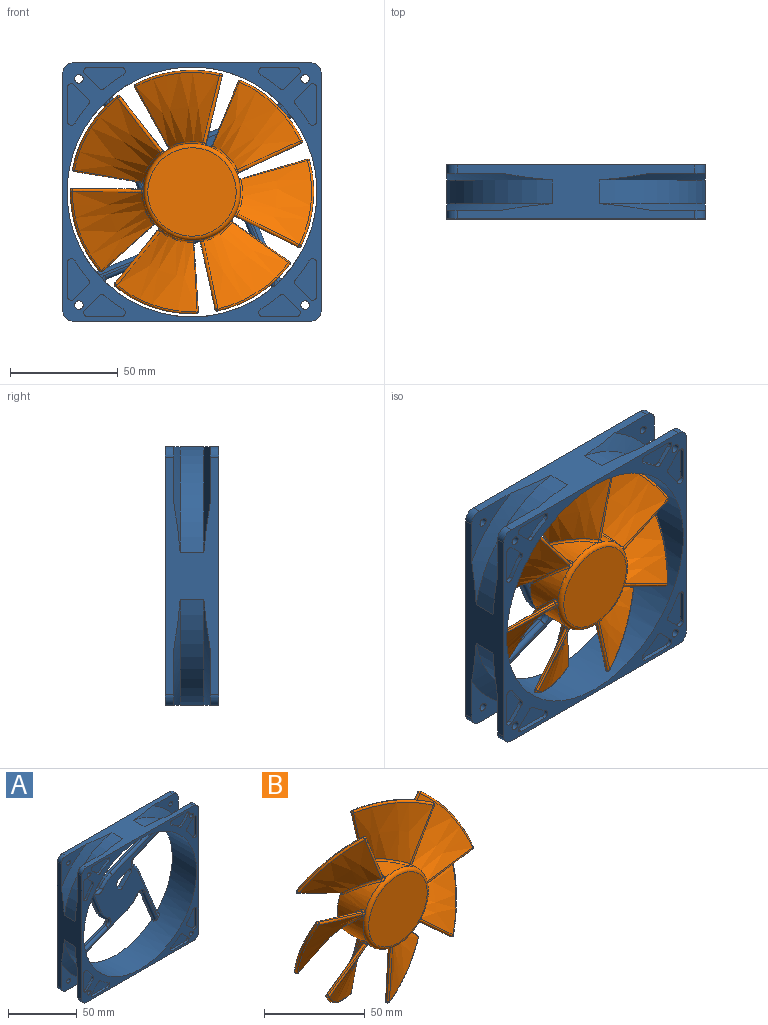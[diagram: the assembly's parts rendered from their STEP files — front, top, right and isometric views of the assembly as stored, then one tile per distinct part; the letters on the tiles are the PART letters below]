
ASSEMBLY  parts=2 mates=1
PART A: 223 faces, bbox 135.7x25x135.7 mm
  f0: plane 88.49x86.45mm, normal (0,-1,0), area 1656.3mm2, adj f15,f184,f185,f186,f187,f196,f197,f198
  f1: plane 120x120mm, normal (0,1,0), area 4802mm2, adj f2,f3,f5,f11,f12,f13,f14,f15
  f2: plane 110x25mm, normal (1,0,0), area 1352.3mm2, adj f1,f6,f23,f24,f25,f26,f27,f28
  f3: plane 6.72x2mm, normal (-1,0,0), area 13.4mm2, adj f1,f4,f35,f192
  f4: plane 65.36x42.4mm, normal (0,1,0), area 561.7mm2, adj f3,f5,f32,f33,f34,f35,f36,f182
  f5: cylinder r=2mm len=2mm, axis (0,1,0), area 1.5mm2, adj f1,f4,f32,f183
  f6: plane 120x120mm, normal (0,-1,0), area 2727.1mm2, adj f2,f7,f8,f9,f10,f12,f13,f14
  f7: cylinder r=2mm len=4mm, axis (0,1,0), area 50.3mm2, adj f6,f31
  f8: cylinder r=2mm len=4mm, axis (0,1,0), area 50.3mm2, adj f6,f26
  f9: cylinder r=2mm len=4mm, axis (0,1,0), area 50.3mm2, adj f6,f24
  f10: cylinder r=2mm len=4mm, axis (0,1,0), area 50.3mm2, adj f6,f21
  f11: plane 11.44x4mm, normal (1,0,0), area 45.8mm2, adj f1,f27,f142,f193
  f12: plane 110x25mm, normal (0,0,1), area 1413.4mm2, adj f1,f6,f26,f27,f28,f29,f30,f31
  f13: plane 110x25mm, normal (-1,0,0), area 1413.4mm2, adj f1,f6,f20,f21,f22,f29,f30,f31
  f14: plane 110x25mm, normal (0,0,-1), area 1413.4mm2, adj f1,f6,f20,f21,f22,f23,f24,f25
  f15: cylinder r=58mm len=116mm, axis (0,1,0), area 8990.7mm2, adj f0,f1,f6,f174,f175,f176,f177,f178
  f16: cylinder r=2mm len=4mm, axis (0,1,0), area 50.3mm2, adj f1,f30
  f17: cylinder r=2mm len=4mm, axis (0,1,0), area 50.3mm2, adj f1,f27
  f18: cylinder r=2mm len=4mm, axis (0,1,0), area 50.3mm2, adj f1,f23
  f19: cylinder r=2mm len=4mm, axis (0,1,0), area 50.3mm2, adj f1,f20
  f20: plane 25.93x25.93mm, normal (0,-1,0), area 257.3mm2, adj f13,f14,f19,f144,f151
  f21: plane 25.93x25.93mm, normal (0,1,0), area 257.3mm2, adj f10,f13,f14,f148,f154
  f22: cylinder r=61mm len=49mm, axis (0,1,0), area 810.7mm2, adj f13,f14,f151,f154
  f23: plane 25.93x25.93mm, normal (0,-1,0), area 257.3mm2, adj f2,f14,f18,f145,f152
  f24: plane 25.93x25.93mm, normal (0,1,0), area 257.3mm2, adj f2,f9,f14,f149,f155
  f25: cylinder r=61mm len=49mm, axis (0,1,0), area 810.7mm2, adj f2,f14,f152,f155
  f26: plane 25.93x25.93mm, normal (0,1,0), area 257.3mm2, adj f2,f8,f12,f146,f156
  f27: plane 25.93x25.93mm, normal (0,-1,0), area 240.5mm2, adj f2,f11,f12,f17,f142,f153,f191,f192
  f28: cylinder r=61mm len=49mm, axis (0,1,0), area 810.7mm2, adj f2,f12,f153,f156
  f29: cylinder r=61mm len=49mm, axis (0,1,0), area 810.7mm2, adj f12,f13,f150,f157
  f30: plane 25.93x25.93mm, normal (0,-1,0), area 257.3mm2, adj f12,f13,f16,f143,f150
  f31: plane 25.93x25.93mm, normal (0,1,0), area 257.3mm2, adj f7,f12,f13,f147,f157
  f32: plane 6.31x6.31mm, normal (0.71,0,-0.71), area 17.9mm2, adj f1,f4,f5,f36
  f33: cylinder r=63mm len=5.42mm, axis (0,1,0), area 13mm2, adj f1,f4,f35,f182
  f34: plane 4.66x2mm, normal (-1,0,0), area 9.3mm2, adj f1,f4,f36,f193
  f35: cylinder r=2mm len=3.72mm, axis (0,1,0), area 10.4mm2, adj f1,f3,f4,f33
  f36: cylinder r=2mm len=3.41mm, axis (0,-1,0), area 9.4mm2, adj f1,f4,f32,f34
  f37: plane 6.31x6.31mm, normal (-0.71,0,0.71), area 17.9mm2, adj f1,f40,f41,f43
  f38: plane 15.22x2mm, normal (0,0,-1), area 30.4mm2, adj f1,f40,f42,f43
  f39: cylinder r=63mm len=8.63mm, axis (0,1,0), area 21.2mm2, adj f1,f40,f41,f42
  f40: plane 19.22x10.31mm, normal (0,1,0), area 129.1mm2, adj f37,f38,f39,f41,f42,f43
  f41: cylinder r=2mm len=2.7mm, axis (0,1,0), area 5.9mm2, adj f1,f37,f39,f40
  f42: cylinder r=2mm len=3.72mm, axis (0,1,0), area 10.4mm2, adj f1,f38,f39,f40
  f43: cylinder r=2mm len=3.41mm, axis (0,-1,0), area 9.4mm2, adj f1,f37,f38,f40
  f44: plane 6.31x6.31mm, normal (-0.71,0,-0.71), area 17.9mm2, adj f1,f47,f48,f50
  f45: cylinder r=63mm len=8.63mm, axis (0,1,0), area 21.2mm2, adj f1,f47,f48,f49
  f46: plane 15.22x2mm, normal (0,0,1), area 30.4mm2, adj f1,f47,f49,f50
  f47: plane 19.22x10.31mm, normal (0,1,0), area 129.1mm2, adj f44,f45,f46,f48,f49,f50
  f48: cylinder r=2mm len=2.7mm, axis (0,1,0), area 5.9mm2, adj f1,f44,f45,f47
  f49: cylinder r=2mm len=3.72mm, axis (0,1,0), area 10.4mm2, adj f1,f45,f46,f47
  f50: cylinder r=2mm len=3.41mm, axis (0,-1,0), area 9.4mm2, adj f1,f44,f46,f47
  f51: plane 6.31x6.31mm, normal (-0.71,0,-0.71), area 17.9mm2, adj f1,f54,f55,f57
  f52: plane 15.22x2mm, normal (1,0,0), area 30.4mm2, adj f1,f54,f56,f57
  f53: cylinder r=63mm len=8.63mm, axis (0,1,0), area 21.2mm2, adj f1,f54,f55,f56
  f54: plane 19.22x10.31mm, normal (0,1,0), area 129.1mm2, adj f51,f52,f53,f55,f56,f57
  f55: cylinder r=2mm len=2.7mm, axis (0,1,0), area 5.9mm2, adj f1,f51,f53,f54
  f56: cylinder r=2mm len=3.72mm, axis (0,1,0), area 10.4mm2, adj f1,f52,f53,f54
  f57: cylinder r=2mm len=3.41mm, axis (0,-1,0), area 9.4mm2, adj f1,f51,f52,f54
  f58: plane 6.31x6.31mm, normal (-0.71,0,0.71), area 17.9mm2, adj f1,f61,f62,f64
  f59: cylinder r=63mm len=8.63mm, axis (0,1,0), area 21.2mm2, adj f1,f61,f62,f63
  f60: plane 15.22x2mm, normal (1,0,0), area 30.4mm2, adj f1,f61,f63,f64
  f61: plane 19.22x10.31mm, normal (0,1,0), area 129.1mm2, adj f58,f59,f60,f62,f63,f64
  f62: cylinder r=2mm len=2.7mm, axis (0,1,0), area 5.9mm2, adj f1,f58,f59,f61
  f63: cylinder r=2mm len=3.72mm, axis (0,1,0), area 10.4mm2, adj f1,f59,f60,f61
  f64: cylinder r=2mm len=3.41mm, axis (0,-1,0), area 9.4mm2, adj f1,f58,f60,f61
  f65: plane 6.31x6.31mm, normal (0.71,0,-0.71), area 17.9mm2, adj f1,f68,f69,f71
  f66: plane 15.22x2mm, normal (0,0,1), area 30.4mm2, adj f1,f68,f70,f71
  f67: cylinder r=63mm len=8.63mm, axis (0,1,0), area 21.2mm2, adj f1,f68,f69,f70
  f68: plane 19.22x10.31mm, normal (0,1,0), area 129.1mm2, adj f65,f66,f67,f69,f70,f71
  f69: cylinder r=2mm len=2.7mm, axis (0,1,0), area 5.9mm2, adj f1,f65,f67,f68
  f70: cylinder r=2mm len=3.72mm, axis (0,1,0), area 10.4mm2, adj f1,f66,f67,f68
  f71: cylinder r=2mm len=3.41mm, axis (0,-1,0), area 9.4mm2, adj f1,f65,f66,f68
  f72: plane 6.31x6.31mm, normal (0.71,0,0.71), area 17.9mm2, adj f1,f75,f76,f78
  f73: cylinder r=63mm len=8.63mm, axis (0,1,0), area 21.2mm2, adj f1,f75,f76,f77
  f74: plane 15.22x2mm, normal (0,0,-1), area 30.4mm2, adj f1,f75,f77,f78
  f75: plane 19.22x10.31mm, normal (0,1,0), area 129.1mm2, adj f72,f73,f74,f76,f77,f78
  f76: cylinder r=2mm len=2.7mm, axis (0,1,0), area 5.9mm2, adj f1,f72,f73,f75
  f77: cylinder r=2mm len=3.72mm, axis (0,1,0), area 10.4mm2, adj f1,f73,f74,f75
  f78: cylinder r=2mm len=3.41mm, axis (0,-1,0), area 9.4mm2, adj f1,f72,f74,f75
  f79: plane 6.31x6.31mm, normal (0.71,0,0.71), area 17.9mm2, adj f1,f82,f83,f85
  f80: plane 15.22x2mm, normal (-1,0,0), area 30.4mm2, adj f1,f82,f84,f85
  f81: cylinder r=63mm len=8.63mm, axis (0,1,0), area 21.2mm2, adj f1,f82,f83,f84
  f82: plane 19.22x10.31mm, normal (0,1,0), area 129.1mm2, adj f79,f80,f81,f83,f84,f85
  f83: cylinder r=2mm len=2.7mm, axis (0,1,0), area 5.9mm2, adj f1,f79,f81,f82
  f84: cylinder r=2mm len=3.72mm, axis (0,1,0), area 10.4mm2, adj f1,f80,f81,f82
  f85: cylinder r=2mm len=3.41mm, axis (0,-1,0), area 9.4mm2, adj f1,f79,f80,f82
  f86: plane 6.31x6.31mm, normal (0.71,0,-0.71), area 17.9mm2, adj f6,f89,f90,f92
  f87: plane 15.22x2mm, normal (-1,0,0), area 30.4mm2, adj f6,f89,f91,f92
  f88: cylinder r=63mm len=8.63mm, axis (0,-1,0), area 21.2mm2, adj f6,f89,f90,f91
  f89: plane 19.22x10.31mm, normal (0,-1,0), area 129.1mm2, adj f86,f87,f88,f90,f91,f92
  f90: cylinder r=2mm len=2.7mm, axis (0,-1,0), area 5.9mm2, adj f6,f86,f88,f89
  f91: cylinder r=2mm len=3.72mm, axis (0,-1,0), area 10.4mm2, adj f6,f87,f88,f89
  f92: cylinder r=2mm len=3.41mm, axis (0,1,0), area 9.4mm2, adj f6,f86,f87,f89
  f93: plane 6.31x6.31mm, normal (-0.71,0,0.71), area 17.9mm2, adj f6,f96,f97,f99
  f94: cylinder r=63mm len=8.63mm, axis (0,-1,0), area 21.2mm2, adj f6,f96,f97,f98
  f95: plane 15.22x2mm, normal (0,0,-1), area 30.4mm2, adj f6,f96,f98,f99
  f96: plane 19.22x10.31mm, normal (0,-1,0), area 129.1mm2, adj f93,f94,f95,f97,f98,f99
  f97: cylinder r=2mm len=2.7mm, axis (0,-1,0), area 5.9mm2, adj f6,f93,f94,f96
  f98: cylinder r=2mm len=3.72mm, axis (0,-1,0), area 10.4mm2, adj f6,f94,f95,f96
  f99: cylinder r=2mm len=3.41mm, axis (0,1,0), area 9.4mm2, adj f6,f93,f95,f96
  f100: plane 6.31x6.31mm, normal (-0.71,0,-0.71), area 17.9mm2, adj f6,f103,f104,f106
  f101: plane 15.22x2mm, normal (0,0,1), area 30.4mm2, adj f6,f103,f105,f106
  f102: cylinder r=63mm len=8.63mm, axis (0,-1,0), area 21.2mm2, adj f6,f103,f104,f105
  f103: plane 19.22x10.31mm, normal (0,-1,0), area 129.1mm2, adj f100,f101,f102,f104,f105,f106
  f104: cylinder r=2mm len=2.7mm, axis (0,-1,0), area 5.9mm2, adj f6,f100,f102,f103
  f105: cylinder r=2mm len=3.72mm, axis (0,-1,0), area 10.4mm2, adj f6,f101,f102,f103
  f106: cylinder r=2mm len=3.41mm, axis (0,1,0), area 9.4mm2, adj f6,f100,f101,f103
  f107: plane 6.31x6.31mm, normal (-0.71,0,-0.71), area 17.9mm2, adj f6,f110,f111,f113
  f108: cylinder r=63mm len=8.63mm, axis (0,-1,0), area 21.2mm2, adj f6,f110,f111,f112
  f109: plane 15.22x2mm, normal (1,0,0), area 30.4mm2, adj f6,f110,f112,f113
  f110: plane 19.22x10.31mm, normal (0,-1,0), area 129.1mm2, adj f107,f108,f109,f111,f112,f113
  f111: cylinder r=2mm len=2.7mm, axis (0,-1,0), area 5.9mm2, adj f6,f107,f108,f110
  f112: cylinder r=2mm len=3.72mm, axis (0,-1,0), area 10.4mm2, adj f6,f108,f109,f110
  f113: cylinder r=2mm len=3.41mm, axis (0,1,0), area 9.4mm2, adj f6,f107,f109,f110
  f114: plane 6.31x6.31mm, normal (-0.71,0,0.71), area 17.9mm2, adj f6,f117,f118,f120
  f115: plane 15.22x2mm, normal (1,0,0), area 30.4mm2, adj f6,f117,f119,f120
  f116: cylinder r=63mm len=8.63mm, axis (0,-1,0), area 21.2mm2, adj f6,f117,f118,f119
  f117: plane 19.22x10.31mm, normal (0,-1,0), area 129.1mm2, adj f114,f115,f116,f118,f119,f120
  f118: cylinder r=2mm len=2.7mm, axis (0,-1,0), area 5.9mm2, adj f6,f114,f116,f117
  f119: cylinder r=2mm len=3.72mm, axis (0,-1,0), area 10.4mm2, adj f6,f115,f116,f117
  f120: cylinder r=2mm len=3.41mm, axis (0,1,0), area 9.4mm2, adj f6,f114,f115,f117
  f121: plane 6.31x6.31mm, normal (0.71,0,-0.71), area 17.9mm2, adj f6,f124,f125,f127
  f122: cylinder r=63mm len=8.63mm, axis (0,-1,0), area 21.2mm2, adj f6,f124,f125,f126
  f123: plane 15.22x2mm, normal (0,0,1), area 30.4mm2, adj f6,f124,f126,f127
  f124: plane 19.22x10.31mm, normal (0,-1,0), area 129.1mm2, adj f121,f122,f123,f125,f126,f127
  f125: cylinder r=2mm len=2.7mm, axis (0,-1,0), area 5.9mm2, adj f6,f121,f122,f124
  f126: cylinder r=2mm len=3.72mm, axis (0,-1,0), area 10.4mm2, adj f6,f122,f123,f124
  f127: cylinder r=2mm len=3.41mm, axis (0,1,0), area 9.4mm2, adj f6,f121,f123,f124
  f128: plane 6.31x6.31mm, normal (0.71,0,0.71), area 17.9mm2, adj f6,f131,f132,f134
  f129: plane 15.22x2mm, normal (0,0,-1), area 30.4mm2, adj f6,f131,f133,f134
  f130: cylinder r=63mm len=8.63mm, axis (0,-1,0), area 21.2mm2, adj f6,f131,f132,f133
  f131: plane 19.22x10.31mm, normal (0,-1,0), area 129.1mm2, adj f128,f129,f130,f132,f133,f134
  f132: cylinder r=2mm len=2.7mm, axis (0,-1,0), area 5.9mm2, adj f6,f128,f130,f131
  f133: cylinder r=2mm len=3.72mm, axis (0,-1,0), area 10.4mm2, adj f6,f129,f130,f131
  f134: cylinder r=2mm len=3.41mm, axis (0,1,0), area 9.4mm2, adj f6,f128,f129,f131
  f135: plane 6.31x6.31mm, normal (0.71,0,0.71), area 17.9mm2, adj f6,f138,f139,f141
  f136: cylinder r=63mm len=8.63mm, axis (0,-1,0), area 21.2mm2, adj f6,f138,f139,f140
  f137: plane 15.22x2mm, normal (-1,0,0), area 30.4mm2, adj f6,f138,f140,f141
  f138: plane 19.22x10.31mm, normal (0,-1,0), area 129.1mm2, adj f135,f136,f137,f139,f140,f141
  f139: cylinder r=2mm len=2.7mm, axis (0,-1,0), area 5.9mm2, adj f6,f135,f136,f138
  f140: cylinder r=2mm len=3.72mm, axis (0,-1,0), area 10.4mm2, adj f6,f136,f137,f138
  f141: cylinder r=2mm len=3.41mm, axis (0,1,0), area 9.4mm2, adj f6,f135,f137,f138
  f142: cylinder r=5mm len=5mm, axis (0,-1,0), area 31.4mm2, adj f1,f11,f12,f27
  f143: cylinder r=5mm len=5mm, axis (0,1,0), area 31.4mm2, adj f1,f12,f13,f30
  f144: cylinder r=5mm len=5mm, axis (0,-1,0), area 31.4mm2, adj f1,f13,f14,f20
  f145: cylinder r=5mm len=5mm, axis (0,1,0), area 31.4mm2, adj f1,f2,f14,f23
  f146: cylinder r=5mm len=5mm, axis (0,-1,0), area 31.4mm2, adj f2,f6,f12,f26
  f147: cylinder r=5mm len=5mm, axis (0,1,0), area 31.4mm2, adj f6,f12,f13,f31
  f148: cylinder r=5mm len=5mm, axis (0,-1,0), area 31.4mm2, adj f6,f13,f14,f21
  f149: cylinder r=5mm len=5mm, axis (0,1,0), area 31.4mm2, adj f2,f6,f14,f24
  f150: cone r=69mm half-angle=69.4deg, axis (0,1,0), area 445.3mm2, adj f12,f13,f29,f30
  f151: cone r=69mm half-angle=69.4deg, axis (0,1,0), area 445.3mm2, adj f13,f14,f20,f22
  f152: cone r=69mm half-angle=69.4deg, axis (0,1,0), area 445.3mm2, adj f2,f14,f23,f25
  f153: cone r=69mm half-angle=69.4deg, axis (0,1,0), area 445.3mm2, adj f2,f12,f27,f28
  f154: cone r=61mm half-angle=69.4deg, axis (0,-1,0), area 445.3mm2, adj f13,f14,f21,f22
  f155: cone r=61mm half-angle=69.4deg, axis (0,-1,0), area 445.3mm2, adj f2,f14,f24,f25
  f156: cone r=61mm half-angle=69.4deg, axis (0,-1,0), area 445.3mm2, adj f2,f12,f26,f28
  f157: cone r=61mm half-angle=69.4deg, axis (0,-1,0), area 445.3mm2, adj f12,f13,f29,f31
  f158: plane 48.09x19.6mm, normal (-0.93,0,-0.38), area 103.9mm2, adj f1,f159,f174,f212
  f159: cylinder r=22.5mm len=10.34mm, axis (0,1,0), area 27.2mm2, adj f1,f158,f170,f213
  f160: plane 31.1x12.68mm, normal (-0.38,0,0.93), area 67.2mm2, adj f1,f170,f175,f215
  f161: plane 48.09x19.6mm, normal (0.38,0,-0.93), area 103.9mm2, adj f1,f162,f176,f218
  f162: cylinder r=22.5mm len=10.34mm, axis (0,1,0), area 27.2mm2, adj f1,f161,f171,f219
  f163: plane 31.1x12.68mm, normal (-0.93,0,-0.38), area 67.2mm2, adj f1,f171,f177,f221
  f164: plane 48.09x19.6mm, normal (0.93,0,0.38), area 103.9mm2, adj f1,f165,f178,f206
  f165: cylinder r=22.5mm len=8.48mm, axis (0,1,0), area 21.1mm2, adj f1,f164,f172,f207
  f166: plane 30.21x12.31mm, normal (0.38,0,-0.93), area 65.2mm2, adj f1,f172,f179,f209
  f167: plane 48.09x19.6mm, normal (-0.38,0,0.93), area 103.9mm2, adj f1,f168,f180,f200
  f168: cylinder r=22.5mm len=10.34mm, axis (0,1,0), area 27.2mm2, adj f1,f167,f173,f201
  f169: plane 31.1x12.68mm, normal (0.93,0,0.38), area 67.2mm2, adj f1,f173,f181,f203
  f170: cylinder r=3mm len=5.29mm, axis (0,1,0), area 13.1mm2, adj f1,f159,f160,f214
  f171: cylinder r=3mm len=5.29mm, axis (0,1,0), area 13.1mm2, adj f1,f162,f163,f220
  f172: cylinder r=3mm len=5.04mm, axis (0,1,0), area 12.2mm2, adj f1,f165,f166,f208
  f173: cylinder r=3mm len=5.29mm, axis (0,1,0), area 13.1mm2, adj f1,f168,f169,f202
  f174: cylinder r=1mm len=2mm, axis (0,1,0), area 4mm2, adj f1,f15,f158,f211
  f175: cylinder r=1mm len=2mm, axis (0,1,0), area 2.6mm2, adj f1,f15,f160,f216
  f176: cylinder r=1mm len=2mm, axis (0,1,0), area 4mm2, adj f1,f15,f161,f217
  f177: cylinder r=1mm len=2mm, axis (0,1,0), area 2.6mm2, adj f1,f15,f163,f222
  f178: cylinder r=1mm len=2mm, axis (0,1,0), area 4mm2, adj f1,f15,f164,f205
  f179: cylinder r=1mm len=2mm, axis (0,1,0), area 2.7mm2, adj f1,f15,f166,f210
  f180: cylinder r=1mm len=2mm, axis (0,1,0), area 4mm2, adj f1,f15,f167,f199
  f181: cylinder r=1mm len=2mm, axis (0,1,0), area 2.6mm2, adj f1,f15,f169,f204
  f182: plane 38.58x15.72mm, normal (-0.38,0,0.93), area 83.3mm2, adj f1,f4,f33,f189
  f183: plane 53.66x21.87mm, normal (0.38,0,-0.93), area 115.9mm2, adj f1,f4,f5,f190
  f184: plane 14.08x5.74mm, normal (0.93,0,0.38), area 39.7mm2, adj f0,f1,f4,f185,f190,f198
  f185: cylinder r=2.5mm len=4.09mm, axis (0,1,0), area 19.8mm2, adj f0,f1,f184,f186
  f186: plane 9.21x9.1mm, normal (-0.71,0,0.7), area 51.8mm2, adj f0,f1,f185,f187
  f187: cylinder r=2.5mm len=4mm, axis (0,1,0), area 11.2mm2, adj f0,f1,f4,f186,f188,f196
  f188: plane 3.81x2mm, normal (-0.93,0,-0.38), area 8.2mm2, adj f1,f4,f187,f189
  f189: cylinder r=2.5mm len=3.26mm, axis (0,1,0), area 7.9mm2, adj f1,f4,f182,f188
  f190: cylinder r=2.5mm len=3.26mm, axis (0,1,0), area 7.9mm2, adj f1,f4,f183,f184
  f191: cylinder r=0.5mm len=2mm, axis (0,1,0), area 1.1mm2, adj f4,f27,f192,f194
  f192: plane 4x3.21mm, normal (0,0,1), area 10.4mm2, adj f1,f2,f3,f4,f27,f191
  f193: plane 4.52x4mm, normal (0,0,-1), area 13mm2, adj f1,f4,f11,f27,f34,f195
  f194: plane 2.83x2mm, normal (0.91,0,0.42), area 6.2mm2, adj f4,f27,f191,f195
  f195: cylinder r=0.5mm len=2mm, axis (0,1,0), area 2mm2, adj f4,f27,f193,f194
  f196: cylinder r=2.5mm len=3.17mm, axis (0,1,0), area 7.4mm2, adj f0,f4,f187,f197
  f197: plane 11.02x4.49mm, normal (0.38,0,-0.93), area 23.8mm2, adj f0,f4,f196,f198
  f198: cylinder r=2.5mm len=3.26mm, axis (0,1,0), area 7.9mm2, adj f0,f4,f184,f197
  f199: torus R=3mm, axis (0,-1,0), area 5.8mm2, adj f0,f15,f180,f200
  f200: cylinder r=2mm len=48.84mm, axis (0.93,0,0.38), area 163.1mm2, adj f0,f167,f199,f201
  f201: torus R=20.5mm, axis (0,-1,0), area 41.4mm2, adj f0,f168,f200,f202
  f202: torus R=5mm, axis (0,-1,0), area 25.5mm2, adj f0,f173,f201,f203
  f203: cylinder r=2mm len=31.85mm, axis (0.38,0,-0.93), area 105.5mm2, adj f0,f169,f202,f204
  f204: torus R=3mm, axis (0,-1,0), area 1.9mm2, adj f0,f15,f181,f203
  f205: torus R=3mm, axis (0,-1,0), area 5.8mm2, adj f0,f15,f178,f206
  f206: cylinder r=2mm len=48.84mm, axis (0.38,0,-0.93), area 163.1mm2, adj f0,f164,f205,f207
  f207: torus R=20.5mm, axis (0,-1,0), area 32mm2, adj f0,f165,f206,f208
  f208: torus R=5mm, axis (0,-1,0), area 23.9mm2, adj f0,f172,f207,f209
  f209: cylinder r=2mm len=30.96mm, axis (-0.93,0,-0.38), area 102.5mm2, adj f0,f166,f208,f210
  f210: torus R=3mm, axis (0,-1,0), area 2.2mm2, adj f0,f15,f179,f209
  f211: torus R=3mm, axis (0,-1,0), area 5.8mm2, adj f0,f15,f174,f212
  f212: cylinder r=2mm len=48.84mm, axis (-0.38,0,0.93), area 163.1mm2, adj f0,f158,f211,f213
  f213: torus R=20.5mm, axis (0,-1,0), area 41.4mm2, adj f0,f159,f212,f214
  f214: torus R=5mm, axis (0,-1,0), area 25.5mm2, adj f0,f170,f213,f215
  f215: cylinder r=2mm len=31.85mm, axis (0.93,0,0.38), area 105.5mm2, adj f0,f160,f214,f216
  f216: torus R=3mm, axis (0,-1,0), area 1.9mm2, adj f0,f15,f175,f215
  f217: torus R=3mm, axis (0,-1,0), area 5.8mm2, adj f0,f15,f176,f218
  f218: cylinder r=2mm len=48.84mm, axis (-0.93,0,-0.38), area 163.1mm2, adj f0,f161,f217,f219
  f219: torus R=20.5mm, axis (0,-1,0), area 41.4mm2, adj f0,f162,f218,f220
  f220: torus R=5mm, axis (0,-1,0), area 25.5mm2, adj f0,f171,f219,f221
  f221: cylinder r=2mm len=31.85mm, axis (-0.38,0,0.93), area 105.5mm2, adj f0,f163,f220,f222
  f222: torus R=3mm, axis (0,-1,0), area 1.9mm2, adj f0,f15,f177,f221
PART B: 129 faces, bbox 116.7x28.3x117.1 mm
  f0: cylinder r=22.5mm len=22.62mm, axis (0,1,0), area 269.8mm2, adj f8,f79,f84,f85,f86,f122,f123
  f1: cylinder r=22.5mm len=28.55mm, axis (0,1,0), area 269.8mm2, adj f8,f79,f80,f81,f91,f92,f93
  f2: cylinder r=22.5mm len=26.16mm, axis (0,1,0), area 269.8mm2, adj f8,f79,f87,f88,f98,f99,f100
  f3: cylinder r=22.5mm len=26.46mm, axis (0,1,0), area 269.8mm2, adj f8,f79,f94,f95,f105,f106,f107
  f4: cylinder r=22.5mm len=28.39mm, axis (0,1,0), area 269.8mm2, adj f8,f79,f101,f102,f112,f113,f114
  f5: cylinder r=22.5mm len=23.05mm, axis (0,1,0), area 269.8mm2, adj f8,f79,f108,f109,f119,f120,f121
  f6: cylinder r=22.5mm len=29.2mm, axis (0,1,0), area 269.8mm2, adj f8,f79,f115,f116,f126,f127,f128
  f7: plane 41x41mm, normal (0,-1,0), area 1320.3mm2, adj f79
  f8: plane 46.45x46.31mm, normal (0,1,0), area 1577.8mm2, adj f0,f1,f2,f3,f4,f5,f6,f12
  f9: bspline ~48.93x45.75mm, area 1053mm2, adj f10,f13,f15,f127
  f10: bspline ~28.41x26.4mm, area 50.3mm2, adj f9,f11,f14,f125,f126
  f11: bspline ~29.49x26.61mm, area 50.5mm2, adj f10,f14,f123,f124
  f12: bspline ~6.61x6.15mm, area 1.2mm2, adj f8,f13,f16
  f13: bspline ~38.34x1.69mm, area 51.8mm2, adj f8,f9,f12,f16,f18,f128
  f14: sphere r=1mm, area 3.6mm2, adj f10,f11,f15,f17
  f15: bspline ~40.08x19.45mm, area 69.1mm2, adj f9,f14,f17,f18
  f16: bspline ~38.36x1.8mm, area 53.5mm2, adj f12,f13,f18
  f17: bspline ~39.97x19.46mm, area 69.1mm2, adj f14,f15,f18
  f18: sphere r=1mm, area 3.3mm2, adj f13,f15,f16,f17
  f19: bspline ~52.59x43.95mm, area 1053mm2, adj f20,f23,f25,f120
  f20: bspline ~37.22x7.01mm, area 50.3mm2, adj f19,f21,f24,f118,f119
  f21: bspline ~38.49x7.24mm, area 50.5mm2, adj f20,f24,f116,f117
  f22: bspline ~6.61x4.49mm, area 1.2mm2, adj f8,f23,f26
  f23: bspline ~30.45x24.61mm, area 51.8mm2, adj f8,f19,f22,f26,f28,f121
  f24: sphere r=1mm, area 3.6mm2, adj f20,f21,f25,f27
  f25: bspline ~37.52x21.97mm, area 69.1mm2, adj f19,f24,f27,f28
  f26: bspline ~31.09x24.61mm, area 53.5mm2, adj f22,f23,f28
  f27: bspline ~37.8x21.41mm, area 69.1mm2, adj f24,f25,f28
  f28: sphere r=1mm, area 3.3mm2, adj f23,f25,f26,f27
  f29: bspline ~53.99x42.68mm, area 1053mm2, adj f30,f33,f35,f113
  f30: bspline ~33.12x19.82mm, area 50.3mm2, adj f29,f31,f34,f111,f112
  f31: bspline ~34.39x19.64mm, area 50.5mm2, adj f30,f34,f109,f110
  f32: bspline ~6.61x6.18mm, area 1.2mm2, adj f8,f33,f36
  f33: bspline ~37.56x9.28mm, area 51.8mm2, adj f8,f29,f32,f36,f38,f114
  f34: sphere r=1mm, area 3.6mm2, adj f30,f31,f35,f37
  f35: bspline ~42.64x19.45mm, area 69.1mm2, adj f29,f34,f37,f38
  f36: bspline ~37.57x10.28mm, area 53.5mm2, adj f32,f33,f38
  f37: bspline ~42.59x19.46mm, area 69.1mm2, adj f34,f35,f38
  f38: sphere r=1mm, area 3.3mm2, adj f33,f35,f36,f37
  f39: bspline ~49.3x47.01mm, area 1053mm2, adj f40,f43,f45,f106
  f40: bspline ~35.33x15.02mm, area 50.3mm2, adj f39,f41,f44,f104,f105
  f41: bspline ~36.28x15.56mm, area 50.5mm2, adj f40,f44,f102,f103
  f42: bspline ~6.61x5.18mm, area 1.2mm2, adj f8,f43,f46
  f43: bspline ~34.87x17.46mm, area 51.8mm2, adj f8,f39,f42,f46,f48,f107
  f44: sphere r=1mm, area 3.6mm2, adj f40,f41,f45,f47
  f45: bspline ~31.83x29.59mm, area 69.1mm2, adj f39,f44,f47,f48
  f46: bspline ~35.32x17.46mm, area 53.5mm2, adj f42,f43,f48
  f47: bspline ~32.38x29.02mm, area 69.1mm2, adj f44,f45,f48
  f48: sphere r=1mm, area 3.3mm2, adj f43,f45,f46,f47
  f49: bspline ~56.34x39.45mm, area 1053mm2, adj f50,f53,f55,f99
  f50: bspline ~36.18x12.25mm, area 50.3mm2, adj f49,f51,f54,f97,f98
  f51: bspline ~37.57x11.67mm, area 50.5mm2, adj f50,f54,f95,f96
  f52: bspline ~6.61x5.9mm, area 1.2mm2, adj f8,f53,f56
  f53: bspline ~34.93x17.32mm, area 51.8mm2, adj f8,f49,f52,f56,f58,f100
  f54: sphere r=1mm, area 3.6mm2, adj f50,f51,f55,f57
  f55: bspline ~43.06x19.45mm, area 69.1mm2, adj f49,f54,f57,f58
  f56: bspline ~34.93x18.25mm, area 53.5mm2, adj f52,f53,f58
  f57: bspline ~43.08x19.46mm, area 69.1mm2, adj f54,f55,f58
  f58: sphere r=1mm, area 3.3mm2, adj f53,f55,f56,f57
  f59: bspline ~49.21x48.75mm, area 1053mm2, adj f60,f63,f65,f92
  f60: bspline ~31.66x22.27mm, area 50.3mm2, adj f59,f61,f64,f90,f91
  f61: bspline ~32.26x23.1mm, area 50.5mm2, adj f60,f64,f88,f89
  f62: bspline ~2.48x2.38mm, area 1.2mm2, adj f8,f63,f66
  f63: bspline ~37.55x9.43mm, area 51.8mm2, adj f8,f59,f62,f66,f68,f93
  f64: sphere r=1mm, area 3.6mm2, adj f60,f61,f65,f67
  f65: bspline ~35.73x24.76mm, area 69.1mm2, adj f59,f64,f67,f68
  f66: bspline ~37.77x9.42mm, area 53.5mm2, adj f62,f63,f68
  f67: bspline ~35.34x25.33mm, area 69.1mm2, adj f64,f65,f68
  f68: sphere r=1mm, area 3.3mm2, adj f63,f65,f66,f67
  f69: bspline ~55.87x39.92mm, area 1053mm2, adj f70,f73,f75,f85
  f70: bspline ~37.41x4.06mm, area 50.3mm2, adj f69,f71,f74,f83,f84
  f71: bspline ~38.87x3.13mm, area 50.5mm2, adj f70,f74,f81,f82
  f72: bspline ~6.61x5.33mm, area 1.2mm2, adj f8,f73,f76
  f73: bspline ~30.54x24.5mm, area 51.8mm2, adj f8,f69,f72,f76,f78,f86
  f74: sphere r=1mm, area 3.6mm2, adj f70,f71,f75,f77
  f75: bspline ~41.32x19.45mm, area 69.1mm2, adj f69,f74,f77,f78
  f76: bspline ~30.54x25.31mm, area 53.5mm2, adj f72,f73,f78
  f77: bspline ~41.41x19.46mm, area 69.1mm2, adj f74,f75,f78
  f78: sphere r=1mm, area 3.3mm2, adj f73,f75,f76,f77
  f79: torus R=20.5mm, axis (0,-1,0), area 424.7mm2, adj f0,f1,f2,f3,f4,f5,f6,f7
  f80: bspline ~22.7x20.9mm, area 32.3mm2, adj f1,f8,f81
  f81: bspline ~3.19x1.39mm, area 3.2mm2, adj f1,f71,f80,f82
  f82: bspline ~1.03x0.73mm, area 0mm2, adj f71,f79,f81,f83
  f83: bspline ~3.15x1.25mm, area 2.8mm2, adj f70,f79,f82,f84
  f84: bspline ~1.11x1.07mm, area 0mm2, adj f0,f70,f83,f85
  f85: bspline ~23.04x20.51mm, area 35.5mm2, adj f0,f69,f84,f86
  f86: bspline ~1.84x1.63mm, area 1.6mm2, adj f0,f8,f73,f85
  f87: bspline ~22.7x16.06mm, area 32.3mm2, adj f2,f8,f88
  f88: bspline ~3.19x1.73mm, area 3.2mm2, adj f2,f61,f87,f89
  f89: bspline ~1.1x0.79mm, area 0mm2, adj f61,f79,f88,f90
  f90: bspline ~2.62x2.15mm, area 2.8mm2, adj f60,f79,f89,f91
  f91: bspline ~1.44x1.07mm, area 0mm2, adj f1,f60,f90,f92
  f92: bspline ~21.6x16.5mm, area 35.5mm2, adj f1,f59,f91,f93
  f93: bspline ~1.84x1.56mm, area 1.6mm2, adj f1,f8,f63,f92
  f94: bspline ~22.7x21mm, area 32.3mm2, adj f3,f8,f95
  f95: bspline ~3.19x1.41mm, area 3.2mm2, adj f3,f51,f94,f96
  f96: bspline ~1.13x0.73mm, area 0mm2, adj f51,f79,f95,f97
  f97: bspline ~3.01x1.69mm, area 2.8mm2, adj f50,f79,f96,f98
  f98: bspline ~1.29x1.07mm, area 0mm2, adj f2,f50,f97,f99
  f99: bspline ~21.6x20.11mm, area 35.5mm2, adj f2,f49,f98,f100
  f100: bspline ~1.84x1.48mm, area 1.6mm2, adj f2,f8,f53,f99
  f101: bspline ~22.7x17.61mm, area 32.3mm2, adj f4,f8,f102
  f102: bspline ~3.19x1.66mm, area 3.2mm2, adj f4,f41,f101,f103
  f103: bspline ~0.97x0.88mm, area 0mm2, adj f41,f79,f102,f104
  f104: bspline ~2.94x1.78mm, area 2.8mm2, adj f40,f79,f103,f105
  f105: bspline ~1.35x1.07mm, area 0mm2, adj f3,f40,f104,f106
  f106: bspline ~21.6x15.79mm, area 35.5mm2, adj f3,f39,f105,f107
  f107: bspline ~1.84x1.67mm, area 1.6mm2, adj f3,f8,f43,f106
  f108: bspline ~22.7x20.17mm, area 32.3mm2, adj f5,f8,f109
  f109: bspline ~3.19x1.6mm, area 3.2mm2, adj f5,f31,f108,f110
  f110: bspline ~1.18x0.73mm, area 0mm2, adj f31,f79,f109,f111
  f111: bspline ~2.73x2.08mm, area 2.8mm2, adj f30,f79,f110,f112
  f112: bspline ~1.41x1.07mm, area 0mm2, adj f4,f30,f111,f113
  f113: bspline ~23.04x21.21mm, area 35.5mm2, adj f4,f29,f112,f114
  f114: bspline ~1.84x1.32mm, area 1.6mm2, adj f4,f8,f33,f113
  f115: bspline ~22.7x19.75mm, area 32.3mm2, adj f6,f8,f116
  f116: bspline ~3.19x1.52mm, area 3.2mm2, adj f6,f21,f115,f117
  f117: bspline ~0.93x0.79mm, area 0mm2, adj f21,f79,f116,f118
  f118: bspline ~3.12x1.32mm, area 2.8mm2, adj f20,f79,f117,f119
  f119: bspline ~1.18x1.07mm, area 0mm2, adj f5,f20,f118,f120
  f120: bspline ~21.6x17.96mm, area 35.5mm2, adj f5,f19,f119,f121
  f121: bspline ~1.84x1.69mm, area 1.6mm2, adj f5,f8,f23,f120
  f122: bspline ~22.7x18.48mm, area 32.3mm2, adj f0,f8,f123
  f123: bspline ~3.19x1.71mm, area 3.2mm2, adj f0,f11,f122,f124
  f124: bspline ~1.17x0.73mm, area 0mm2, adj f11,f79,f123,f125
  f125: bspline ~2.42x2.38mm, area 2.8mm2, adj f10,f79,f124,f126
  f126: bspline ~1.46x1.07mm, area 0mm2, adj f6,f10,f125,f127
  f127: bspline ~21.6x18.66mm, area 35.5mm2, adj f6,f9,f126,f128
  f128: bspline ~1.84x1.38mm, area 1.6mm2, adj f6,f8,f13,f127
PLACE A at identity fixed
PLACE B rot(axis=(0,-1,0),119.1deg) t=(0,0,0)mm
MATE revolute A.f15 <-> B.f0  axis (0,-1,0) through (0,-25,0)mm
